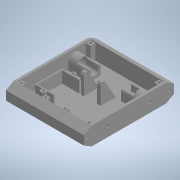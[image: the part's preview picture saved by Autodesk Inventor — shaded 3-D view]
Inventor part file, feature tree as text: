
AUTODESK INVENTOR PART (.ipt)
format: ipt  version: 2020 (Build 240168000, 168)  size: 504,832 bytes
history: native  units: in
note: dims shown in document units (in); Inventor stores cm internally (conversion verified against a paired STEP export)
features: sketch x15, projected_geometry x15, extrude x14, mirror x4, plane x2
ambient origin geometry x8: Origin, YZ Plane, XZ Plane, XY Plane, X Axis, Y Axis, Z Axis, Center Point
bodies: Solid1 (feature_tree)
feature tree (50):
  extrude  "Extrusion1"  Depth=5.9055in
  extrude  "Extrusion2"  TaperAngle=0.0deg  [1 undecoded]
  extrude  "Extrusion3"  Depth=1.063in
  extrude  "Extrusion4"  Depth=0.315in
  extrude  "Extrusion5"  TaperAngle=0.0deg  [1 undecoded]
  extrude  "Extrusion6"  Depth=0.5906in
  mirror  "Mirror1"
  extrude  "Extrusion7"  Depth=0.0787in
  mirror  "Mirror2"
  extrude  "Extrusion8"  Depth=0.6102in
  mirror  "Mirror3"
  plane  "Work Plane1"
  extrude  "Extrusion9"  Depth=0.7874in TaperAngle=0.0deg
  mirror  "Mirror4"
  extrude  "Extrusion10"  Depth=6.063in TaperAngle=0.0deg
  extrude  "Extrusion11"  Depth=0.1575in
  extrude  "Extrusion12"  TaperAngle=0.0deg  [1 undecoded]
  extrude  "Extrusion13"  Depth=0.2756in
  extrude  "Extrusion14"  Depth=0.4331in
  plane  "Work Plane2"
  sketch  "Sketch18"  dims[d34=0.122in d38=2.7559in d40=0.061in d41=0.0909in d42=0.2362in d43=0.0in d44=60.0deg d45=0.0787in d46=0.315in d48=0.993in d49=0.0in d51=0.1575in d52=0.1575in d53=0.2756in d54=0.0in d55=0.4724in d56=1.2008in d57=1.6142in d58=1.5945in d59=0.0787in d60=0.0787in d62=0.315in d63=0.7677in d64=0.0in d65=0.1575in d66=0.1575in d67=0.2756in d68=0.0in d69=0.8268in d70=0.2953in d71=0.0394in d72=0.0in d76=0.1575in d77=120.0deg d79=0.1969in d80=0.1969in d81=0.1969in d82=0.1969in d83=0.1969in d85=120.0deg]
  sketch  "Sketch1"  dims[d0=1.1811in d1=5.9055in]
  sketch  "Sketch2"  dims[d2=5.1181in d3=0.0in]
  projected_geometry  "Projected Loop1"
  sketch  "Sketch3"  dims[d4=0.1575in d5=1.063in]
  projected_geometry  "Projected Loop2"
  projected_geometry  "Projected Loop3"
  sketch  "Sketch4"  dims[d6=0.0in d8=0.315in]
  sketch  "Sketch5"  dims[d10=0.993in d11=0.0in]
  projected_geometry  "Projected Loop4"
  sketch  "Sketch6"  dims[d12=0.6496in d13=0.5906in]
  sketch  "Sketch7"  dims[d14=1.5748in d15=0.0787in]
  sketch  "Sketch9"  dims[d16=0.5512in d17=0.0in d18=0.6102in]
  sketch  "Sketch10"  dims[d19=0.4803in d20=0.7874in d21=0.0in]
  sketch  "Sketch12"  dims[d22=0.1654in d23=6.063in d24=0.0in]
  projected_geometry  "Projected Loop6"
  projected_geometry  "Projected Loop7"
  projected_geometry  "Projected Loop8"
  sketch  "Sketch13"  dims[d25=0.5114in d26=0.1575in]
  projected_geometry  "Projected Loop9"
  projected_geometry  "Projected Loop10"
  projected_geometry  "Projected Loop11"
  projected_geometry  "Projected Loop12"
  projected_geometry  "Projected Loop13"
  projected_geometry  "Projected Loop14"
  sketch  "Sketch14"  dims[d27=1.5748in d28=0.0in d29=0.0in]
  sketch  "Sketch15"  dims[d30=0.1575in d31=0.2756in]
  projected_geometry  "Projected Loop15"
  sketch  "Sketch16"  dims[d32=0.0in d33=0.4331in]
  projected_geometry  "Projected Loop18"
note: 3 required parameter values undecoded (feature->parameter linkage not recoverable at this tier; creation-order binding heuristic only, values carry confidence <= 0.55)
